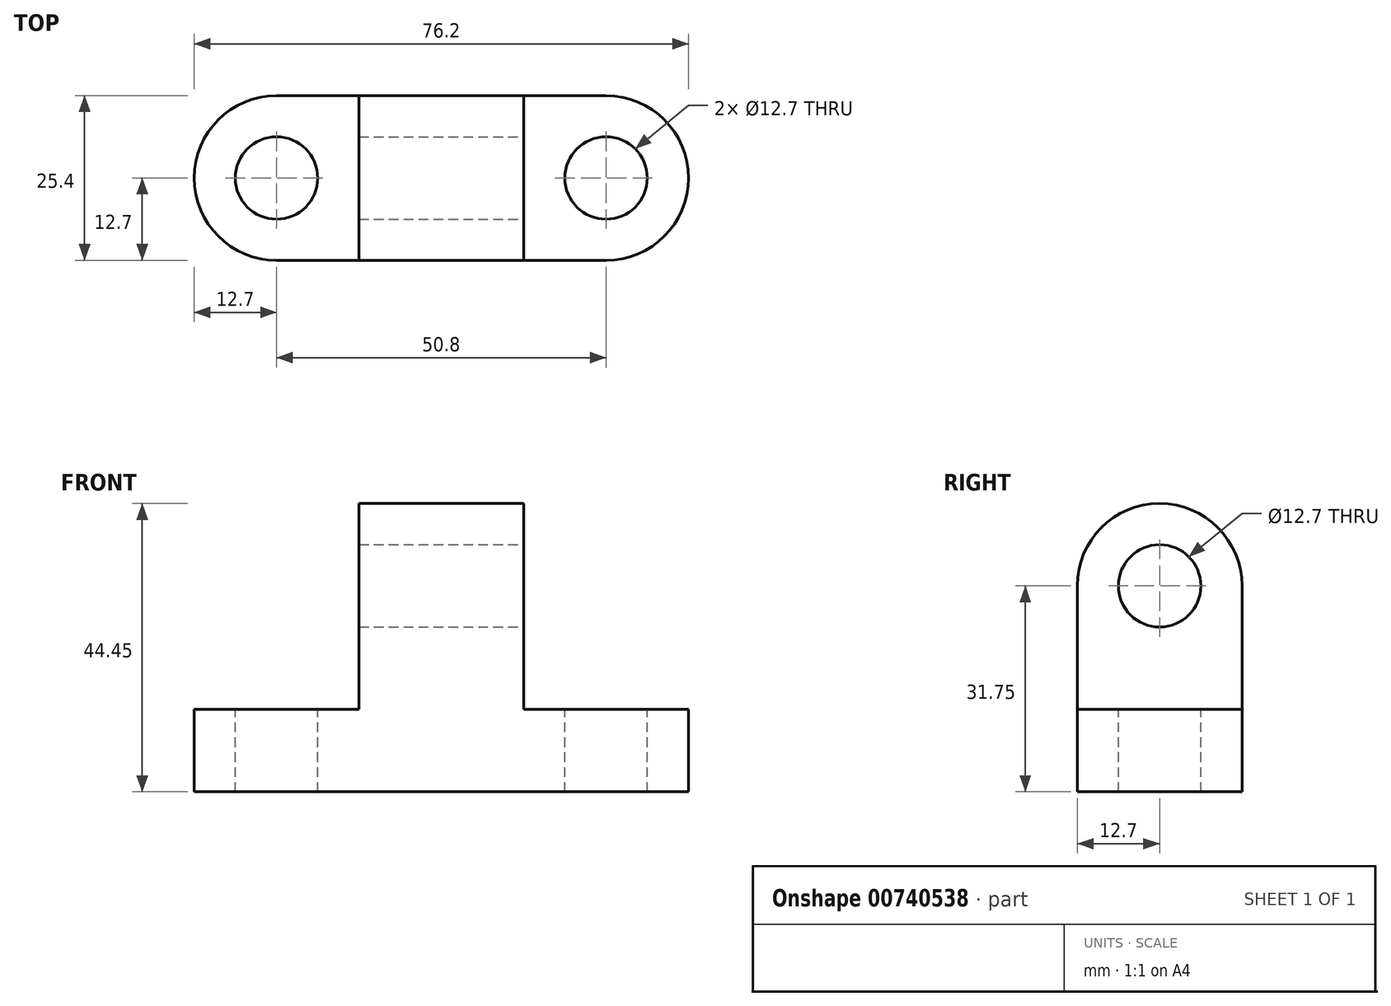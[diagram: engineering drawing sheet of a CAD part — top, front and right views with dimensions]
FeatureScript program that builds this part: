
annotation { "Feature Type Name" : "Feature", "Feature Type Description" : "" }
export const myFeature = defineFeature(function(context is Context, id is Id, definition is map)
    precondition{}
    {
        {
            var Q0;
            Q0=qCreatedBy(makeId("Right.planeOp"),FACE);
            var sketch = newSketch(context, id + "F0", { "sketchPlane" : qUnion([Q0])});
            skLineSegment(sketch, "E0.bottom", {"start": v(0, 0) * mm, "end": v(-25.4, 0) * mm});
            skLineSegment(sketch, "E0.top", {"start": v(0, 31.75) * mm, "end": v(-25.4, 31.75) * mm});
            skLineSegment(sketch, "E0.left", {"start": v(0, 0) * mm, "end": v(0, 31.75) * mm});
            skLineSegment(sketch, "E0.right", {"start": v(-25.4, 0) * mm, "end": v(-25.4, 31.75) * mm});
            skCircle(sketch, "E1", {"center": v(-12.7, 31.75) * mm, "radius": 12.7 * mm});
            skSolve(sketch);
        }
        {
            var Q0;
            {var subQ0=sQuery(id+"F0.wireOp",EDGE,"E0.top");Q0=makeQuery(id+"F0.imprint","IMPRINT",FACE,{"disambiguationData":[TD([[makeQuery(id+"F0.imprint","IMPRINT",EDGE,{"derivedFrom":subQ0}),-1.0]])]});}
            var Q1;
            {var subQ0=sQuery(id+"F0.wireOp",EDGE,"E0.top");Q1=makeQuery(id+"F0.imprint","IMPRINT",FACE,{"disambiguationData":[TD([[makeQuery(id+"F0.imprint","IMPRINT",EDGE,{"derivedFrom":subQ0}),1.0]])]});}
            var Q2;
            Q2=makeQuery(id+"F0.imprint","IMPRINT",FACE,{"disambiguationData":[TD([[makeQuery(id+"F0.imprint","IMPRINT",EDGE,{"derivedFrom":sQuery(id+"F0.wireOp",EDGE,"E0.bottom")}),-1.0]])]});
            extrude(context, id + "F1", {"entities" : qUnion([Q0, Q1, Q2]), "depth" : 25.4 * mm, "offsetDistance" : 25.4 * mm});
        }
        {
            var Q0;
            Q0=qCreatedBy(makeId("Top.planeOp"),FACE);
            var sketch = newSketch(context, id + "F2", { "sketchPlane" : qUnion([Q0])});
            skLineSegment(sketch, "E2.bottom", {"start": v(0, 0) * mm, "end": v(-12.7, 0) * mm});
            skLineSegment(sketch, "E2.top", {"start": v(0, -25.4) * mm, "end": v(-12.7, -25.4) * mm});
            skLineSegment(sketch, "E2.left", {"start": v(0, 0) * mm, "end": v(0, -25.4) * mm});
            skLineSegment(sketch, "E2.right", {"start": v(-12.7, 0) * mm, "end": v(-12.7, -25.4) * mm});
            skCircle(sketch, "E3", {"center": v(-12.7, -12.7) * mm, "radius": 12.7 * mm});
            skLineSegment(sketch, "E4.bottom", {"start": v(25.4, 0) * mm, "end": v(38.1, 0) * mm});
            skLineSegment(sketch, "E4.top", {"start": v(25.4, -25.4) * mm, "end": v(38.1, -25.4) * mm});
            skLineSegment(sketch, "E4.left", {"start": v(25.4, 0) * mm, "end": v(25.4, -25.4) * mm});
            skLineSegment(sketch, "E4.right", {"start": v(38.1, 0) * mm, "end": v(38.1, -25.4) * mm});
            skCircle(sketch, "E5", {"center": v(38.1, -12.7) * mm, "radius": 12.7 * mm});
            skSolve(sketch);
        }
        {
            var Q0;
            {var subQ0=sQuery(id+"F2.wireOp",EDGE,"E2.right");Q0=makeQuery(id+"F2.imprint","IMPRINT",FACE,{"disambiguationData":[TD([[makeQuery(id+"F2.imprint","IMPRINT",EDGE,{"derivedFrom":subQ0}),-1.0]])]});}
            var Q1;
            {var subQ0=sQuery(id+"F2.wireOp",EDGE,"E2.right");Q1=makeQuery(id+"F2.imprint","IMPRINT",FACE,{"disambiguationData":[TD([[makeQuery(id+"F2.imprint","IMPRINT",EDGE,{"derivedFrom":subQ0}),1.0]])]});}
            var Q2;
            {var subQ0=sQuery(id+"F2.wireOp",EDGE,"E2.bottom");Q2=makeQuery(id+"F2.imprint","IMPRINT",FACE,{"disambiguationData":[TD([[makeQuery(id+"F2.imprint","IMPRINT",EDGE,{"derivedFrom":subQ0}),1.0]])]});}
            var Q3;
            {var subQ0=sQuery(id+"F2.wireOp",EDGE,"E2.top");Q3=makeQuery(id+"F2.imprint","IMPRINT",FACE,{"disambiguationData":[TD([[makeQuery(id+"F2.imprint","IMPRINT",EDGE,{"derivedFrom":subQ0}),-1.0]])]});}
            var Q4;
            {var subQ0=sQuery(id+"F2.wireOp",EDGE,"E4.right");Q4=makeQuery(id+"F2.imprint","IMPRINT",FACE,{"disambiguationData":[TD([[makeQuery(id+"F2.imprint","IMPRINT",EDGE,{"derivedFrom":subQ0}),-1.0]])]});}
            var Q5;
            {var subQ0=sQuery(id+"F2.wireOp",EDGE,"E4.bottom");Q5=makeQuery(id+"F2.imprint","IMPRINT",FACE,{"disambiguationData":[TD([[makeQuery(id+"F2.imprint","IMPRINT",EDGE,{"derivedFrom":subQ0}),-1.0]])]});}
            var Q6;
            {var subQ0=sQuery(id+"F2.wireOp",EDGE,"E4.top");Q6=makeQuery(id+"F2.imprint","IMPRINT",FACE,{"disambiguationData":[TD([[makeQuery(id+"F2.imprint","IMPRINT",EDGE,{"derivedFrom":subQ0}),1.0]])]});}
            var Q7;
            {var subQ0=sQuery(id+"F2.wireOp",EDGE,"E4.right");Q7=makeQuery(id+"F2.imprint","IMPRINT",FACE,{"disambiguationData":[TD([[makeQuery(id+"F2.imprint","IMPRINT",EDGE,{"derivedFrom":subQ0}),1.0]])]});}
            extrude(context, id + "F3", {"entities" : qUnion([Q0, Q1, Q2, Q3, Q4, Q5, Q6, Q7]), "operationType" : NewBodyOperationType.ADD, "depth" : 12.7 * mm, "offsetDistance" : 25.4 * mm});
        }
        {
            var Q0;
            Q0=makeQuery(id+"F1.opExtrude","CAP_FACE",FACE,{"disambiguationData":[OSD([sQuery(id+"F0.wireOp",EDGE,"E0.bottom"),sQuery(id+"F0.wireOp",EDGE,"E0.left"),sQuery(id+"F0.wireOp",EDGE,"E0.right"),sQuery(id+"F0.wireOp",EDGE,"E1")])],"isStart":false});
            var sketch = newSketch(context, id + "F4", { "sketchPlane" : qUnion([Q0])});
            skCircle(sketch, "E6", {"center": v(-12.7, 31.75) * mm, "radius": 6.35 * mm});
            skSolve(sketch);
        }
        {
            var Q0;
            Q0=makeQuery(id+"F4.imprint","IMPRINT",FACE,{"disambiguationData":[TD([[makeQuery(id+"F4.imprint","IMPRINT",EDGE,{"derivedFrom":sQuery(id+"F4.wireOp",EDGE,"E6")}),1.0]])]});
            extrude(context, id + "F5", {"entities" : qUnion([Q0]), "operationType" : NewBodyOperationType.REMOVE, "oppositeDirection" : true, "depth" : 25.4 * mm, "offsetDistance" : 25.4 * mm});
        }
        {
            var Q0;
            Q0=makeQuery(id+"F3.opExtrude","CAP_FACE",FACE,{"disambiguationData":[OSD([sQuery(id+"F2.wireOp",EDGE,"E2.bottom"),sQuery(id+"F2.wireOp",EDGE,"E2.top"),sQuery(id+"F2.wireOp",EDGE,"E2.left"),sQuery(id+"F2.wireOp",EDGE,"E3")])],"isStart":false});
            var sketch = newSketch(context, id + "F6", { "sketchPlane" : qUnion([Q0])});
            skCircle(sketch, "E7", {"center": v(-12.7, -12.7) * mm, "radius": 6.35 * mm});
            skSolve(sketch);
        }
        {
            var Q0;
            Q0=makeQuery(id+"F6.imprint","IMPRINT",FACE,{"disambiguationData":[TD([[makeQuery(id+"F6.imprint","IMPRINT",EDGE,{"derivedFrom":sQuery(id+"F6.wireOp",EDGE,"E7")}),1.0]])]});
            extrude(context, id + "F7", {"entities" : qUnion([Q0]), "operationType" : NewBodyOperationType.REMOVE, "oppositeDirection" : true, "depth" : 12.7 * mm, "offsetDistance" : 25.4 * mm});
        }
        {
            var Q0;
            Q0=makeQuery(id+"F3.opExtrude","CAP_FACE",FACE,{"disambiguationData":[OSD([sQuery(id+"F2.wireOp",EDGE,"E4.bottom"),sQuery(id+"F2.wireOp",EDGE,"E4.top"),sQuery(id+"F2.wireOp",EDGE,"E4.left"),sQuery(id+"F2.wireOp",EDGE,"E5")])],"isStart":false});
            var sketch = newSketch(context, id + "F8", { "sketchPlane" : qUnion([Q0])});
            skCircle(sketch, "E8", {"center": v(38.1, -12.7) * mm, "radius": 6.35 * mm});
            skSolve(sketch);
        }
        {
            var Q0;
            Q0=makeQuery(id+"F8.imprint","IMPRINT",FACE,{"disambiguationData":[TD([[makeQuery(id+"F8.imprint","IMPRINT",EDGE,{"derivedFrom":sQuery(id+"F8.wireOp",EDGE,"E8")}),1.0]])]});
            extrude(context, id + "F9", {"entities" : qUnion([Q0]), "operationType" : NewBodyOperationType.REMOVE, "oppositeDirection" : true, "depth" : 12.7 * mm, "offsetDistance" : 25.4 * mm});
        }
    });
